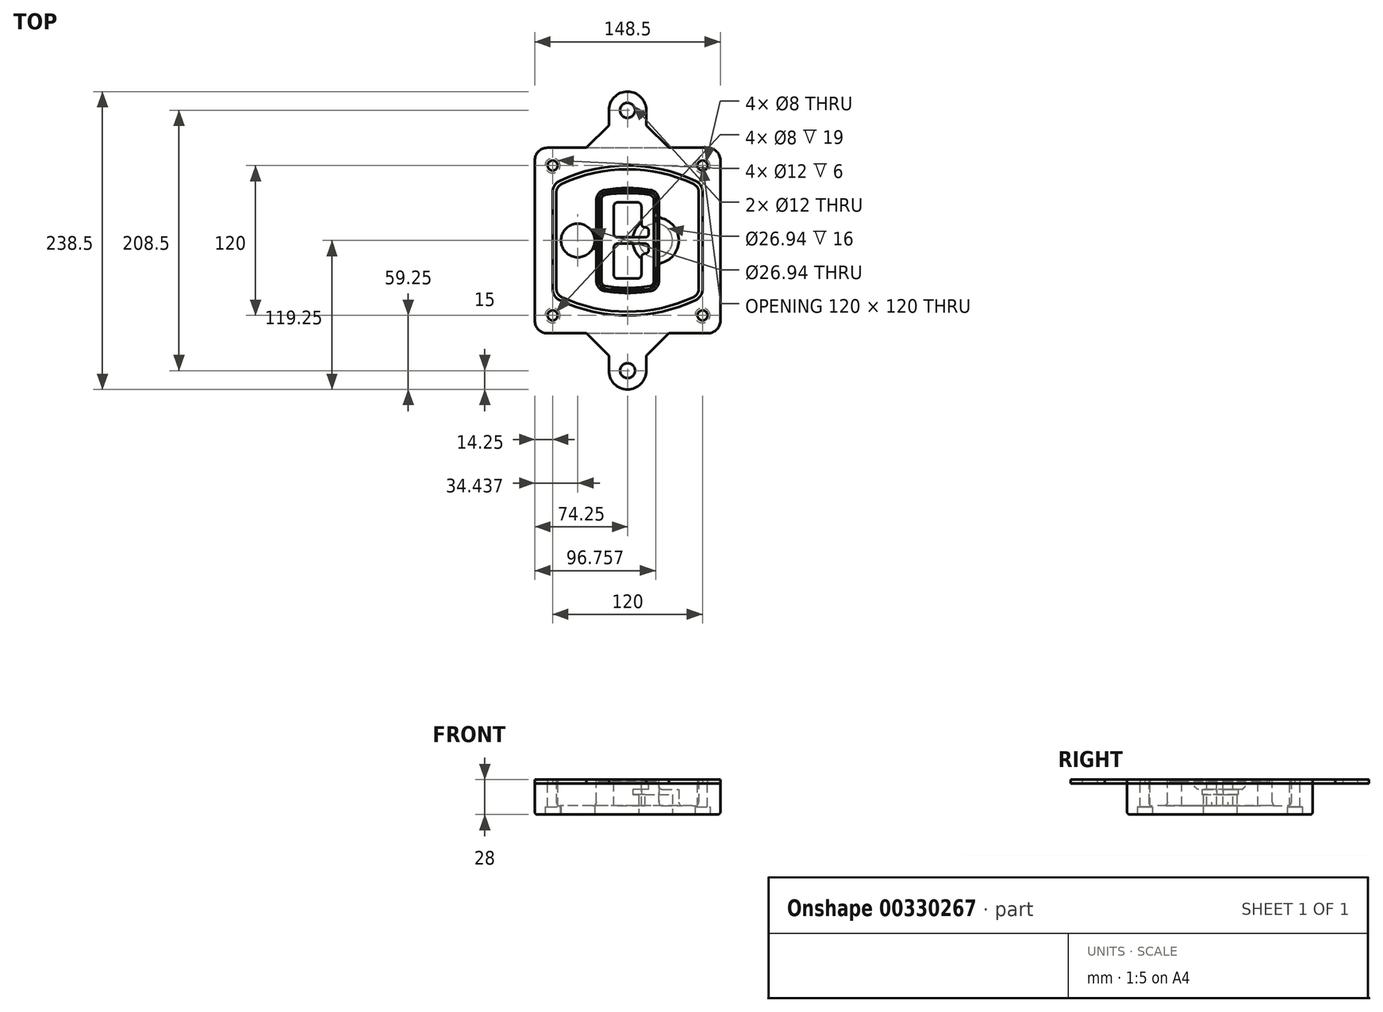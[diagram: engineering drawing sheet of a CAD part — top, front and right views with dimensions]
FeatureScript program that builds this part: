
annotation { "Feature Type Name" : "Feature", "Feature Type Description" : "" }
export const myFeature = defineFeature(function(context is Context, id is Id, definition is map)
    precondition{}
    {
        {
            var Q0;
            Q0=qCreatedBy(makeId("Top.planeOp"),FACE);
            var sketch = newSketch(context, id + "F0", { "sketchPlane" : qUnion([Q0])});
            skPoint(sketch, "E0.rect.middle", {"position": v(0, 0) * mm});
            skLineSegment(sketch, "E1.bottom", {"start": v(-64.25, -74.25) * mm, "end": v(64.25, -74.25) * mm});
            skLineSegment(sketch, "E1.top", {"start": v(-64.25, 74.25) * mm, "end": v(64.25, 74.25) * mm});
            skLineSegment(sketch, "E1.left", {"start": v(-74.25, -64.25) * mm, "end": v(-74.25, 64.25) * mm});
            skLineSegment(sketch, "E1.right", {"start": v(74.25, -64.25) * mm, "end": v(74.25, 64.25) * mm});
            skLineSegment(sketch, "E2", {"start": v(-74.25, 74.25) * mm, "end": v(74.25, -74.25) * mm, "construction": true});
            skLineSegment(sketch, "E3", {"start": v(74.25, 74.25) * mm, "end": v(-74.25, -74.25) * mm, "construction": true});
            skCircle(sketch, "E4", {"center": v(-60, 60) * mm, "radius": 4 * mm});
            skCircle(sketch, "E5", {"center": v(60, 60) * mm, "radius": 4 * mm});
            skCircle(sketch, "E6", {"center": v(60, -60) * mm, "radius": 4 * mm});
            skCircle(sketch, "E7", {"center": v(-60, -60) * mm, "radius": 4 * mm});
            skLineSegment(sketch, "E8", {"start": v(-60, 60) * mm, "end": v(60, 60) * mm, "construction": true});
            skLineSegment(sketch, "E9", {"start": v(60, 60) * mm, "end": v(60, -60) * mm, "construction": true});
            skLineSegment(sketch, "E10", {"start": v(60, -60) * mm, "end": v(-60, -60) * mm, "construction": true});
            skLineSegment(sketch, "E11", {"start": v(-60, -60) * mm, "end": v(-60, 60) * mm, "construction": true});
            skLineSegment(sketch, "E12", {"start": v(-60, 38.83) * mm, "end": v(-60, -38.83) * mm});
            skLineSegment(sketch, "E13", {"start": v(60, 38.83) * mm, "end": v(60, -38.83) * mm});
            skArc(sketch, "E14", {"start": v(54.26, 47.88) * mm, "mid": v(0, 60) * mm, "end": v(-54.26, 47.88) * mm});
            skArc(sketch, "E15", {"start": v(-54.26, -47.88) * mm, "mid": v(0, -60) * mm, "end": v(54.26, -47.88) * mm});
            skLineSegment(sketch, "E16", {"start": v(-60, 0) * mm, "end": v(60, 0) * mm, "construction": true});
            skPoint(sketch, "E17.visualSharp", {"position": v(-60, -45) * mm});
            skArc(sketch, "E17.filletArc", {"start": v(-60, -38.83) * mm, "mid": v(-58.44, -44.2) * mm, "end": v(-54.26, -47.88) * mm});
            skPoint(sketch, "E18.visualSharp", {"position": v(-60, 45) * mm});
            skArc(sketch, "E18.filletArc", {"start": v(-54.26, 47.88) * mm, "mid": v(-58.44, 44.2) * mm, "end": v(-60, 38.83) * mm});
            skPoint(sketch, "E19.visualSharp", {"position": v(60, 45) * mm});
            skArc(sketch, "E19.filletArc", {"start": v(60, 38.83) * mm, "mid": v(58.44, 44.2) * mm, "end": v(54.26, 47.88) * mm});
            skPoint(sketch, "E20.visualSharp", {"position": v(60, -45) * mm});
            skArc(sketch, "E20.filletArc", {"start": v(54.26, -47.88) * mm, "mid": v(58.44, -44.2) * mm, "end": v(60, -38.83) * mm});
            skPoint(sketch, "E21.visualSharp", {"position": v(-74.25, 74.25) * mm});
            skArc(sketch, "E21.filletArc", {"start": v(-64.25, 74.25) * mm, "mid": v(-71.32, 71.32) * mm, "end": v(-74.25, 64.25) * mm});
            skPoint(sketch, "E22.visualSharp", {"position": v(74.25, 74.25) * mm});
            skArc(sketch, "E22.filletArc", {"start": v(74.25, 64.25) * mm, "mid": v(71.32, 71.32) * mm, "end": v(64.25, 74.25) * mm});
            skPoint(sketch, "E23.visualSharp", {"position": v(74.25, -74.25) * mm});
            skArc(sketch, "E23.filletArc", {"start": v(64.25, -74.25) * mm, "mid": v(71.32, -71.32) * mm, "end": v(74.25, -64.25) * mm});
            skPoint(sketch, "E24.visualSharp", {"position": v(-74.25, -74.25) * mm});
            skArc(sketch, "E24.filletArc", {"start": v(-74.25, -64.25) * mm, "mid": v(-71.32, -71.32) * mm, "end": v(-64.25, -74.25) * mm});
            skArc(sketch, "E25.0", {"start": v(57, 38.83) * mm, "mid": v(55.9, 42.58) * mm, "end": v(52.98, 45.17) * mm});
            skLineSegment(sketch, "E25.1", {"start": v(57, 38.83) * mm, "end": v(57, -38.83) * mm});
            skArc(sketch, "E25.2", {"start": v(52.98, -45.17) * mm, "mid": v(55.9, -42.58) * mm, "end": v(57, -38.83) * mm});
            skArc(sketch, "E25.3", {"start": v(-52.98, -45.17) * mm, "mid": v(0, -57) * mm, "end": v(52.98, -45.17) * mm});
            skArc(sketch, "E25.4", {"start": v(-57, -38.83) * mm, "mid": v(-55.9, -42.58) * mm, "end": v(-52.98, -45.17) * mm});
            skArc(sketch, "E25.5", {"start": v(52.98, 45.17) * mm, "mid": v(0, 57) * mm, "end": v(-52.98, 45.17) * mm});
            skLineSegment(sketch, "E25.6", {"start": v(-57, 38.83) * mm, "end": v(-57, -38.83) * mm});
            skArc(sketch, "E25.7", {"start": v(-52.98, 45.17) * mm, "mid": v(-55.9, 42.58) * mm, "end": v(-57, 38.83) * mm});
            skArc(sketch, "E26.0", {"start": v(-55.96, 51.5) * mm, "mid": v(-61.82, 46.33) * mm, "end": v(-64, 38.83) * mm});
            skArc(sketch, "E26.1", {"start": v(55.96, 51.5) * mm, "mid": v(0, 64) * mm, "end": v(-55.96, 51.5) * mm});
            skArc(sketch, "E26.2", {"start": v(64, 38.83) * mm, "mid": v(61.82, 46.33) * mm, "end": v(55.96, 51.5) * mm});
            skLineSegment(sketch, "E26.3", {"start": v(64, 38.83) * mm, "end": v(64, -38.83) * mm});
            skArc(sketch, "E26.4", {"start": v(55.96, -51.5) * mm, "mid": v(61.82, -46.33) * mm, "end": v(64, -38.83) * mm});
            skLineSegment(sketch, "E26.5", {"start": v(-64, 38.83) * mm, "end": v(-64, -38.83) * mm});
            skArc(sketch, "E26.6", {"start": v(-55.96, -51.5) * mm, "mid": v(0, -64) * mm, "end": v(55.96, -51.5) * mm});
            skArc(sketch, "E26.7", {"start": v(-64, -38.83) * mm, "mid": v(-61.82, -46.33) * mm, "end": v(-55.96, -51.5) * mm});
            skSolve(sketch);
        }
        {
            var Q0;
            Q0=makeQuery(id+"F0.imprint","IMPRINT",FACE,{"disambiguationData":[TD([[makeQuery(id+"F0.imprint","IMPRINT",EDGE,{"derivedFrom":sQuery(id+"F0.wireOp",EDGE,"E1.bottom")}),1.0]])]});
            var Q1;
            Q1=makeQuery(id+"F0.imprint","IMPRINT",FACE,{"disambiguationData":[TD([[makeQuery(id+"F0.imprint","IMPRINT",EDGE,{"derivedFrom":sQuery(id+"F0.wireOp",EDGE,"E12")}),1.0]])]});
            var Q2;
            Q2=makeQuery(id+"F0.imprint","IMPRINT",FACE,{"disambiguationData":[TD([[makeQuery(id+"F0.imprint","IMPRINT",EDGE,{"derivedFrom":sQuery(id+"F0.wireOp",EDGE,"E25.0")}),1.0]])]});
            var Q3;
            Q3=makeQuery(id+"F0.imprint","IMPRINT",FACE,{"disambiguationData":[TD([[makeQuery(id+"F0.imprint","IMPRINT",EDGE,{"derivedFrom":sQuery(id+"F0.wireOp",EDGE,"E12")}),-1.0]])]});
            extrude(context, id + "F1", {"entities" : qUnion([Q0, Q1, Q2, Q3]), "oppositeDirection" : true, "depth" : 25 * mm});
        }
        {
            var Q0;
            Q0=makeQuery(id+"F0.imprint","IMPRINT",FACE,{"disambiguationData":[TD([[makeQuery(id+"F0.imprint","IMPRINT",EDGE,{"derivedFrom":sQuery(id+"F0.wireOp",EDGE,"E12")}),1.0]])]});
            extrude(context, id + "F2", {"entities" : qUnion([Q0]), "operationType" : NewBodyOperationType.ADD, "depth" : 3 * mm});
        }
        {
            var Q0;
            Q0=makeQuery(id+"F0.imprint","IMPRINT",FACE,{"disambiguationData":[TD([[makeQuery(id+"F0.imprint","IMPRINT",EDGE,{"derivedFrom":sQuery(id+"F0.wireOp",EDGE,"E25.0")}),1.0]])]});
            extrude(context, id + "F3", {"entities" : qUnion([Q0]), "operationType" : NewBodyOperationType.REMOVE, "oppositeDirection" : true, "depth" : 18 * mm});
        }
        {
            var Q0;
            Q0=makeQuery(id+"F2.opExtrude","CAP_FACE",FACE,{"disambiguationData":[OSD([sQuery(id+"F0.wireOp",EDGE,"E12"),sQuery(id+"F0.wireOp",EDGE,"E13"),sQuery(id+"F0.wireOp",EDGE,"E14"),sQuery(id+"F0.wireOp",EDGE,"E15"),sQuery(id+"F0.wireOp",EDGE,"E17.filletArc"),sQuery(id+"F0.wireOp",EDGE,"E18.filletArc"),sQuery(id+"F0.wireOp",EDGE,"E19.filletArc"),sQuery(id+"F0.wireOp",EDGE,"E20.filletArc"),sQuery(id+"F0.wireOp",EDGE,"E25.0"),sQuery(id+"F0.wireOp",EDGE,"E25.1"),sQuery(id+"F0.wireOp",EDGE,"E25.2"),sQuery(id+"F0.wireOp",EDGE,"E25.3"),sQuery(id+"F0.wireOp",EDGE,"E25.4"),sQuery(id+"F0.wireOp",EDGE,"E25.5"),sQuery(id+"F0.wireOp",EDGE,"E25.6"),sQuery(id+"F0.wireOp",EDGE,"E25.7")])],"isStart":false});
            var sketch = newSketch(context, id + "F4", { "sketchPlane" : qUnion([Q0])});
            skArc(sketch, "E27.0", {"start": v(-18.34, -40.45) * mm, "mid": v(0, -42) * mm, "end": v(18.34, -40.45) * mm});
            skArc(sketch, "E28.0", {"start": v(18.34, 40.45) * mm, "mid": v(0, 42) * mm, "end": v(-18.34, 40.45) * mm});
            skLineSegment(sketch, "E29", {"start": v(-25, 32.57) * mm, "end": v(-25, -32.57) * mm});
            skLineSegment(sketch, "E30", {"start": v(25, 32.57) * mm, "end": v(25, -32.57) * mm});
            skLineSegment(sketch, "E31", {"start": v(-25, 39.1) * mm, "end": v(25, 39.1) * mm, "construction": true});
            skLineSegment(sketch, "E32", {"start": v(-25, -39.1) * mm, "end": v(25, -39.1) * mm, "construction": true});
            skPoint(sketch, "E33.visualSharp", {"position": v(-25, 39.1) * mm});
            skArc(sketch, "E33.filletArc", {"start": v(-18.34, 40.45) * mm, "mid": v(-23.11, 37.73) * mm, "end": v(-25, 32.57) * mm});
            skPoint(sketch, "E34.visualSharp", {"position": v(25, 39.1) * mm});
            skArc(sketch, "E34.filletArc", {"start": v(25, 32.57) * mm, "mid": v(23.11, 37.73) * mm, "end": v(18.34, 40.45) * mm});
            skPoint(sketch, "E35.visualSharp", {"position": v(25, -39.1) * mm});
            skArc(sketch, "E35.filletArc", {"start": v(18.34, -40.45) * mm, "mid": v(23.11, -37.73) * mm, "end": v(25, -32.57) * mm});
            skPoint(sketch, "E36.visualSharp", {"position": v(-25, -39.1) * mm});
            skArc(sketch, "E36.filletArc", {"start": v(-25, -32.57) * mm, "mid": v(-23.11, -37.73) * mm, "end": v(-18.34, -40.45) * mm});
            skArc(sketch, "E37.0", {"start": v(52.98, 45.17) * mm, "mid": v(0, 57) * mm, "end": v(-52.98, 45.17) * mm});
            skArc(sketch, "E37.1", {"start": v(-52.98, 45.17) * mm, "mid": v(-55.9, 42.58) * mm, "end": v(-57, 38.83) * mm});
            skLineSegment(sketch, "E37.2", {"start": v(-57, 38.83) * mm, "end": v(-57, -38.83) * mm});
            skArc(sketch, "E37.3", {"start": v(-57, -38.83) * mm, "mid": v(-55.9, -42.58) * mm, "end": v(-52.98, -45.17) * mm});
            skArc(sketch, "E37.4", {"start": v(-52.98, -45.17) * mm, "mid": v(0, -57) * mm, "end": v(52.98, -45.17) * mm});
            skArc(sketch, "E37.5", {"start": v(52.98, -45.17) * mm, "mid": v(55.9, -42.58) * mm, "end": v(57, -38.83) * mm});
            skLineSegment(sketch, "E37.6", {"start": v(57, 38.83) * mm, "end": v(57, -38.83) * mm});
            skArc(sketch, "E37.7", {"start": v(57, 38.83) * mm, "mid": v(55.9, 42.58) * mm, "end": v(52.98, 45.17) * mm});
            skLineSegment(sketch, "E38.0", {"start": v(23, 32.57) * mm, "end": v(23, -32.57) * mm});
            skArc(sketch, "E38.1", {"start": v(18, -38.48) * mm, "mid": v(21.58, -36.44) * mm, "end": v(23, -32.57) * mm});
            skArc(sketch, "E38.2", {"start": v(-18, -38.48) * mm, "mid": v(0, -40) * mm, "end": v(18, -38.48) * mm});
            skArc(sketch, "E38.3", {"start": v(-23, -32.57) * mm, "mid": v(-21.58, -36.44) * mm, "end": v(-18, -38.48) * mm});
            skLineSegment(sketch, "E38.4", {"start": v(-23, 32.57) * mm, "end": v(-23, -32.57) * mm});
            skArc(sketch, "E38.5", {"start": v(23, 32.57) * mm, "mid": v(21.58, 36.44) * mm, "end": v(18, 38.48) * mm});
            skArc(sketch, "E38.6", {"start": v(-18, 38.48) * mm, "mid": v(-21.58, 36.44) * mm, "end": v(-23, 32.57) * mm});
            skArc(sketch, "E38.7", {"start": v(18, 38.48) * mm, "mid": v(0, 40) * mm, "end": v(-18, 38.48) * mm});
            skArc(sketch, "E39.0", {"start": v(21, 32.57) * mm, "mid": v(20.06, 35.15) * mm, "end": v(17.67, 36.5) * mm});
            skLineSegment(sketch, "E39.1", {"start": v(21, 32.57) * mm, "end": v(21, -32.57) * mm});
            skArc(sketch, "E39.2", {"start": v(17.67, -36.5) * mm, "mid": v(20.06, -35.15) * mm, "end": v(21, -32.57) * mm});
            skArc(sketch, "E39.3", {"start": v(-17.67, -36.5) * mm, "mid": v(0, -38) * mm, "end": v(17.67, -36.5) * mm});
            skArc(sketch, "E39.4", {"start": v(-21, -32.57) * mm, "mid": v(-20.06, -35.15) * mm, "end": v(-17.67, -36.5) * mm});
            skArc(sketch, "E39.5", {"start": v(17.67, 36.5) * mm, "mid": v(0, 38) * mm, "end": v(-17.67, 36.5) * mm});
            skLineSegment(sketch, "E39.6", {"start": v(-21, 32.57) * mm, "end": v(-21, -32.57) * mm});
            skArc(sketch, "E39.7", {"start": v(-17.67, 36.5) * mm, "mid": v(-20.06, 35.15) * mm, "end": v(-21, 32.57) * mm});
            skLineSegment(sketch, "E40", {"start": v(-25, 0) * mm, "end": v(25, 0) * mm, "construction": true});
            skLineSegment(sketch, "E41", {"start": v(-11, 5.5) * mm, "end": v(-11, 27.5) * mm});
            skLineSegment(sketch, "E42", {"start": v(-8, 30.5) * mm, "end": v(8, 30.5) * mm});
            skLineSegment(sketch, "E43", {"start": v(11, 27.5) * mm, "end": v(11, 13.5) * mm});
            skLineSegment(sketch, "E44", {"start": v(14, 10.5) * mm, "end": v(14, 10.5) * mm});
            skLineSegment(sketch, "E45", {"start": v(17, 7.5) * mm, "end": v(17, 5.5) * mm});
            skLineSegment(sketch, "E46", {"start": v(14, 2.5) * mm, "end": v(-8, 2.5) * mm});
            skPoint(sketch, "E47.visualSharp", {"position": v(-11, 30.5) * mm});
            skArc(sketch, "E47.filletArc", {"start": v(-8, 30.5) * mm, "mid": v(-10.12, 29.62) * mm, "end": v(-11, 27.5) * mm});
            skPoint(sketch, "E48.visualSharp", {"position": v(11, 30.5) * mm});
            skArc(sketch, "E48.filletArc", {"start": v(11, 27.5) * mm, "mid": v(10.12, 29.62) * mm, "end": v(8, 30.5) * mm});
            skPoint(sketch, "E49.visualSharp", {"position": v(11, 10.5) * mm});
            skArc(sketch, "E49.filletArc", {"start": v(11, 13.5) * mm, "mid": v(11.88, 11.38) * mm, "end": v(14, 10.5) * mm});
            skPoint(sketch, "E50.visualSharp", {"position": v(17, 10.5) * mm});
            skArc(sketch, "E50.filletArc", {"start": v(17, 7.5) * mm, "mid": v(16.12, 9.62) * mm, "end": v(14, 10.5) * mm});
            skPoint(sketch, "E51.visualSharp", {"position": v(17, 2.5) * mm});
            skArc(sketch, "E51.filletArc", {"start": v(14, 2.5) * mm, "mid": v(16.12, 3.38) * mm, "end": v(17, 5.5) * mm});
            skPoint(sketch, "E52.visualSharp", {"position": v(-11, 2.5) * mm});
            skArc(sketch, "E52.filletArc", {"start": v(-11, 5.5) * mm, "mid": v(-10.12, 3.38) * mm, "end": v(-8, 2.5) * mm});
            skLineSegment(sketch, "E53.0.MirrorCS", {"start": v(14, -2.5) * mm, "end": v(-8, -2.5) * mm});
            skArc(sketch, "E54.0.MirrorCS", {"start": v(-11, -5.5) * mm, "mid": v(-10.12, -3.38) * mm, "end": v(-8, -2.5) * mm});
            skLineSegment(sketch, "E55.0.MirrorCS", {"start": v(-11, -5.5) * mm, "end": v(-11, -27.5) * mm});
            skArc(sketch, "E56.0.MirrorCS", {"start": v(-8, -30.5) * mm, "mid": v(-10.12, -29.62) * mm, "end": v(-11, -27.5) * mm});
            skLineSegment(sketch, "E57.0.MirrorCS", {"start": v(-8, -30.5) * mm, "end": v(8, -30.5) * mm});
            skArc(sketch, "E58.0.MirrorCS", {"start": v(11, -27.5) * mm, "mid": v(10.12, -29.62) * mm, "end": v(8, -30.5) * mm});
            skLineSegment(sketch, "E59.0.MirrorCS", {"start": v(11, -27.5) * mm, "end": v(11, -13.5) * mm});
            skArc(sketch, "E60.0.MirrorCS", {"start": v(11, -13.5) * mm, "mid": v(11.88, -11.38) * mm, "end": v(14, -10.5) * mm});
            skArc(sketch, "E61.0.MirrorCS", {"start": v(17, -7.5) * mm, "mid": v(16.12, -9.62) * mm, "end": v(14, -10.5) * mm});
            skLineSegment(sketch, "E62.0.MirrorCS", {"start": v(17, -7.5) * mm, "end": v(17, -5.5) * mm});
            skArc(sketch, "E63.0.MirrorCS", {"start": v(14, -2.5) * mm, "mid": v(16.12, -3.38) * mm, "end": v(17, -5.5) * mm});
            skSolve(sketch);
        }
        {
            var Q0;
            Q0=makeQuery(id+"F4.imprint","IMPRINT",FACE,{"disambiguationData":[TD([[makeQuery(id+"F4.imprint","IMPRINT",EDGE,{"derivedFrom":sQuery(id+"F4.wireOp",EDGE,"E27.0")}),1.0]])]});
            var Q1;
            Q1=makeQuery(id+"F4.imprint","IMPRINT",FACE,{"disambiguationData":[TD([[makeQuery(id+"F4.imprint","IMPRINT",EDGE,{"derivedFrom":sQuery(id+"F4.wireOp",EDGE,"E38.0")}),-1.0]])]});
            var Q2;
            Q2=makeQuery(id+"F4.imprint","IMPRINT",FACE,{"disambiguationData":[TD([[makeQuery(id+"F4.imprint","IMPRINT",EDGE,{"derivedFrom":sQuery(id+"F4.wireOp",EDGE,"E39.0")}),1.0]])]});
            extrude(context, id + "F5", {"entities" : qUnion([Q0, Q1, Q2]), "operationType" : NewBodyOperationType.ADD, "endBound" : BoundingType.UP_TO_NEXT, "oppositeDirection" : true, "depth" : 25 * mm});
        }
        {
            var Q0;
            Q0=makeQuery(id+"F4.imprint","IMPRINT",FACE,{"disambiguationData":[TD([[makeQuery(id+"F4.imprint","IMPRINT",EDGE,{"derivedFrom":sQuery(id+"F4.wireOp",EDGE,"E38.0")}),-1.0]])]});
            extrude(context, id + "F6", {"entities" : qUnion([Q0]), "operationType" : NewBodyOperationType.REMOVE, "oppositeDirection" : true, "depth" : 2 * mm});
        }
        {
            var Q0;
            Q0=makeQuery(id+"F1.opExtrude","CAP_FACE",FACE,{"disambiguationData":[OSD([sQuery(id+"F0.wireOp",EDGE,"E1.bottom"),sQuery(id+"F0.wireOp",EDGE,"E1.top"),sQuery(id+"F0.wireOp",EDGE,"E1.left"),sQuery(id+"F0.wireOp",EDGE,"E1.right"),sQuery(id+"F0.wireOp",EDGE,"E4"),sQuery(id+"F0.wireOp",EDGE,"E5"),sQuery(id+"F0.wireOp",EDGE,"E6"),sQuery(id+"F0.wireOp",EDGE,"E7"),sQuery(id+"F0.wireOp",EDGE,"E21.filletArc"),sQuery(id+"F0.wireOp",EDGE,"E22.filletArc"),sQuery(id+"F0.wireOp",EDGE,"E23.filletArc"),sQuery(id+"F0.wireOp",EDGE,"E24.filletArc")])],"isStart":false});
            var sketch = newSketch(context, id + "F7", { "sketchPlane" : qUnion([Q0])});
            skCircle(sketch, "E64", {"center": v(22.5, 0) * mm, "radius": 13.47 * mm});
            skCircle(sketch, "E65", {"center": v(-39.81, 0) * mm, "radius": 13.47 * mm});
            skLineSegment(sketch, "E66", {"start": v(74.25, 0) * mm, "end": v(-74.25, 0) * mm});
            skCircle(sketch, "E67", {"center": v(22.5, 0) * mm, "radius": 18.47 * mm});
            skCircle(sketch, "E68", {"center": v(60, -60) * mm, "radius": 6 * mm});
            skCircle(sketch, "E69", {"center": v(-60, -60) * mm, "radius": 6 * mm});
            skCircle(sketch, "E70", {"center": v(-60, 60) * mm, "radius": 6 * mm});
            skCircle(sketch, "E71", {"center": v(60, 60) * mm, "radius": 6 * mm});
            skSolve(sketch);
        }
        {
            var Q0;
            {var subQ1=sQuery(id+"F7.wireOp",EDGE,"E66");var subQ4=sQuery(id+"F7.wireOp",EDGE,"E64");var subQ6=makeQuery(id+"F7.imprint","INTERSECT",VERTEX,{"disambiguationData":[OD(0.0)],"derivedFrom":[subQ4,subQ1]});Q0=makeQuery(id+"F7.imprint","IMPRINT",FACE,{"disambiguationData":[TD([[makeQuery(id+"F7.imprint","IMPRINT",EDGE,{"disambiguationData":[TD([[subQ6,-1.0]])],"derivedFrom":subQ4}),-1.0]])]});}
            var Q1;
            {var subQ0=sQuery(id+"F7.wireOp",EDGE,"E66");var subQ1=sQuery(id+"F7.wireOp",EDGE,"E64");var subQ3=makeQuery(id+"F7.imprint","INTERSECT",VERTEX,{"disambiguationData":[OD(0.0)],"derivedFrom":[subQ1,subQ0]});Q1=makeQuery(id+"F7.imprint","IMPRINT",FACE,{"disambiguationData":[TD([[makeQuery(id+"F7.imprint","IMPRINT",EDGE,{"disambiguationData":[TD([[subQ3,-1.0]])],"derivedFrom":subQ1}),1.0]])]});}
            var Q2;
            {var subQ0=sQuery(id+"F7.wireOp",EDGE,"E66");var subQ1=sQuery(id+"F7.wireOp",EDGE,"E64");var subQ3=makeQuery(id+"F7.imprint","INTERSECT",VERTEX,{"disambiguationData":[OD(0.0)],"derivedFrom":[subQ1,subQ0]});Q2=makeQuery(id+"F7.imprint","IMPRINT",FACE,{"disambiguationData":[TD([[makeQuery(id+"F7.imprint","IMPRINT",EDGE,{"disambiguationData":[TD([[subQ3,1.0]])],"derivedFrom":subQ1}),1.0]])]});}
            var Q3;
            {var subQ1=sQuery(id+"F7.wireOp",EDGE,"E66");var subQ4=sQuery(id+"F7.wireOp",EDGE,"E64");var subQ6=makeQuery(id+"F7.imprint","INTERSECT",VERTEX,{"disambiguationData":[OD(0.0)],"derivedFrom":[subQ4,subQ1]});Q3=makeQuery(id+"F7.imprint","IMPRINT",FACE,{"disambiguationData":[TD([[makeQuery(id+"F7.imprint","IMPRINT",EDGE,{"disambiguationData":[TD([[subQ6,1.0]])],"derivedFrom":subQ4}),-1.0]])]});}
            extrude(context, id + "F8", {"entities" : qUnion([Q0, Q1, Q2, Q3]), "operationType" : NewBodyOperationType.ADD, "oppositeDirection" : true, "depth" : 20 * mm});
        }
        {
            var Q0;
            {var subQ0=sQuery(id+"F7.wireOp",EDGE,"E66");var subQ1=sQuery(id+"F7.wireOp",EDGE,"E64");var subQ3=makeQuery(id+"F7.imprint","INTERSECT",VERTEX,{"disambiguationData":[OD(0.0)],"derivedFrom":[subQ1,subQ0]});Q0=makeQuery(id+"F7.imprint","IMPRINT",FACE,{"disambiguationData":[TD([[makeQuery(id+"F7.imprint","IMPRINT",EDGE,{"disambiguationData":[TD([[subQ3,-1.0]])],"derivedFrom":subQ1}),1.0]])]});}
            var Q1;
            {var subQ0=sQuery(id+"F7.wireOp",EDGE,"E66");var subQ1=sQuery(id+"F7.wireOp",EDGE,"E64");var subQ3=makeQuery(id+"F7.imprint","INTERSECT",VERTEX,{"disambiguationData":[OD(0.0)],"derivedFrom":[subQ1,subQ0]});Q1=makeQuery(id+"F7.imprint","IMPRINT",FACE,{"disambiguationData":[TD([[makeQuery(id+"F7.imprint","IMPRINT",EDGE,{"disambiguationData":[TD([[subQ3,1.0]])],"derivedFrom":subQ1}),1.0]])]});}
            extrude(context, id + "F9", {"entities" : qUnion([Q0, Q1]), "operationType" : NewBodyOperationType.REMOVE, "oppositeDirection" : true, "depth" : 16 * mm});
        }
        {
            var Q0;
            {var subQ0=sQuery(id+"F7.wireOp",EDGE,"E66");var subQ1=sQuery(id+"F7.wireOp",EDGE,"E65");var subQ3=makeQuery(id+"F7.imprint","INTERSECT",VERTEX,{"disambiguationData":[OD(0.0)],"derivedFrom":[subQ1,subQ0]});Q0=makeQuery(id+"F7.imprint","IMPRINT",FACE,{"disambiguationData":[TD([[makeQuery(id+"F7.imprint","IMPRINT",EDGE,{"disambiguationData":[TD([[subQ3,-1.0]])],"derivedFrom":subQ1}),1.0]])]});}
            var Q1;
            {var subQ0=sQuery(id+"F7.wireOp",EDGE,"E66");var subQ1=sQuery(id+"F7.wireOp",EDGE,"E65");var subQ3=makeQuery(id+"F7.imprint","INTERSECT",VERTEX,{"disambiguationData":[OD(0.0)],"derivedFrom":[subQ1,subQ0]});Q1=makeQuery(id+"F7.imprint","IMPRINT",FACE,{"disambiguationData":[TD([[makeQuery(id+"F7.imprint","IMPRINT",EDGE,{"disambiguationData":[TD([[subQ3,1.0]])],"derivedFrom":subQ1}),1.0]])]});}
            extrude(context, id + "F10", {"entities" : qUnion([Q0, Q1]), "operationType" : NewBodyOperationType.REMOVE, "oppositeDirection" : true, "depth" : 25 * mm});
        }
        {
            var Q0;
            Q0=makeQuery(id+"F7.imprint","IMPRINT",FACE,{"disambiguationData":[TD([[makeQuery(id+"F7.imprint","IMPRINT",EDGE,{"derivedFrom":sQuery(id+"F7.wireOp",EDGE,"E68")}),1.0]])]});
            var Q1;
            Q1=makeQuery(id+"F7.imprint","IMPRINT",FACE,{"disambiguationData":[TD([[makeQuery(id+"F7.imprint","IMPRINT",EDGE,{"derivedFrom":makeQuery(id+"F1.opExtrude","CAP_EDGE",EDGE,{"disambiguationData":[OSD([sQuery(id+"F0.wireOp",EDGE,"E5")])],"isStart":false})}),-1.0]])]});
            var Q2;
            Q2=makeQuery(id+"F7.imprint","IMPRINT",FACE,{"disambiguationData":[TD([[makeQuery(id+"F7.imprint","IMPRINT",EDGE,{"derivedFrom":sQuery(id+"F7.wireOp",EDGE,"E69")}),1.0]])]});
            var Q3;
            Q3=makeQuery(id+"F7.imprint","IMPRINT",FACE,{"disambiguationData":[TD([[makeQuery(id+"F7.imprint","IMPRINT",EDGE,{"derivedFrom":makeQuery(id+"F1.opExtrude","CAP_EDGE",EDGE,{"disambiguationData":[OSD([sQuery(id+"F0.wireOp",EDGE,"E4")])],"isStart":false})}),-1.0]])]});
            var Q4;
            Q4=makeQuery(id+"F7.imprint","IMPRINT",FACE,{"disambiguationData":[TD([[makeQuery(id+"F7.imprint","IMPRINT",EDGE,{"derivedFrom":sQuery(id+"F7.wireOp",EDGE,"E70")}),1.0]])]});
            var Q5;
            Q5=makeQuery(id+"F7.imprint","IMPRINT",FACE,{"disambiguationData":[TD([[makeQuery(id+"F7.imprint","IMPRINT",EDGE,{"derivedFrom":makeQuery(id+"F1.opExtrude","CAP_EDGE",EDGE,{"disambiguationData":[OSD([sQuery(id+"F0.wireOp",EDGE,"E7")])],"isStart":false})}),-1.0]])]});
            var Q6;
            Q6=makeQuery(id+"F7.imprint","IMPRINT",FACE,{"disambiguationData":[TD([[makeQuery(id+"F7.imprint","IMPRINT",EDGE,{"derivedFrom":sQuery(id+"F7.wireOp",EDGE,"E71")}),1.0]])]});
            var Q7;
            Q7=makeQuery(id+"F7.imprint","IMPRINT",FACE,{"disambiguationData":[TD([[makeQuery(id+"F7.imprint","IMPRINT",EDGE,{"derivedFrom":makeQuery(id+"F1.opExtrude","CAP_EDGE",EDGE,{"disambiguationData":[OSD([sQuery(id+"F0.wireOp",EDGE,"E6")])],"isStart":false})}),-1.0]])]});
            extrude(context, id + "F11", {"entities" : qUnion([Q0, Q1, Q2, Q3, Q4, Q5, Q6, Q7]), "operationType" : NewBodyOperationType.REMOVE, "oppositeDirection" : true, "depth" : 6 * mm});
        }
        {
            var Q0;
            Q0=makeQuery(id+"F9.boolean.opBoolean","COPY",FACE,{"derivedFrom":makeQuery(id+"F9.opExtrude","CAP_FACE",FACE,{"disambiguationData":[OSD([sQuery(id+"F7.wireOp",EDGE,"E64")])],"isStart":false})});
            var sketch = newSketch(context, id + "F12", { "sketchPlane" : qUnion([Q0])});
            skArc(sketch, "E72.0", {"start": v(11, 14.45) * mm, "mid": v(6.45, 9.13) * mm, "end": v(4.2, 2.5) * mm});
            skArc(sketch, "E72.1", {"start": v(4.2, -2.5) * mm, "mid": v(6.45, -9.13) * mm, "end": v(11, -14.45) * mm});
            skLineSegment(sketch, "E73", {"start": v(4.2, -2.5) * mm, "end": v(14, -2.5) * mm});
            skLineSegment(sketch, "E74.0", {"start": v(14, 2.5) * mm, "end": v(4.2, 2.5) * mm});
            skArc(sketch, "E74.1", {"start": v(14, 2.5) * mm, "mid": v(16.12, 3.38) * mm, "end": v(17, 5.5) * mm});
            skLineSegment(sketch, "E74.2", {"start": v(17, 7.5) * mm, "end": v(17, 5.5) * mm});
            skArc(sketch, "E74.3", {"start": v(17, 7.5) * mm, "mid": v(16.12, 9.62) * mm, "end": v(14, 10.5) * mm});
            skArc(sketch, "E74.4", {"start": v(11, 13.5) * mm, "mid": v(11.88, 11.38) * mm, "end": v(14, 10.5) * mm});
            skLineSegment(sketch, "E74.5", {"start": v(11, 14.45) * mm, "end": v(11, 13.5) * mm});
            skLineSegment(sketch, "E74.7", {"start": v(14, -2.5) * mm, "end": v(4.2, -2.5) * mm});
            skArc(sketch, "E74.8", {"start": v(14, -2.5) * mm, "mid": v(16.12, -3.38) * mm, "end": v(17, -5.5) * mm});
            skLineSegment(sketch, "E74.9", {"start": v(17, -7.5) * mm, "end": v(17, -5.5) * mm});
            skArc(sketch, "E74.10", {"start": v(17, -7.5) * mm, "mid": v(16.12, -9.62) * mm, "end": v(14, -10.5) * mm});
            skArc(sketch, "E74.11", {"start": v(11, -13.5) * mm, "mid": v(11.88, -11.38) * mm, "end": v(14, -10.5) * mm});
            skLineSegment(sketch, "E74.12", {"start": v(11, -14.45) * mm, "end": v(11, -13.5) * mm});
            skPoint(sketch, "E75.orphan", {"position": v(11, -27.5) * mm});
            skPoint(sketch, "E76.orphan", {"position": v(-8, -2.5) * mm});
            skPoint(sketch, "E77.orphan", {"position": v(-8, 2.5) * mm});
            skPoint(sketch, "E78.orphan", {"position": v(11, 27.5) * mm});
            skSolve(sketch);
        }
        {
            var Q0;
            {var subQ7=sQuery(id+"F12.wireOp",EDGE,"E72.0");var subQ14=sQuery(id+"F12.wireOp",EDGE,"E72.1");var subQ16=sQuery(id+"F12.wireOp",EDGE,"E74.1");var subQ18=sQuery(id+"F12.wireOp",EDGE,"E74.8");Q0=qUnion([makeQuery(id+"F12.imprint","IMPRINT",FACE,{"disambiguationData":[TD([[makeQuery(id+"F12.imprint","IMPRINT",EDGE,{"derivedFrom":subQ7}),1.0]])]}),makeQuery(id+"F12.imprint","IMPRINT",FACE,{"disambiguationData":[TD([[makeQuery(id+"F12.imprint","IMPRINT",EDGE,{"derivedFrom":subQ14}),1.0]])]}),makeQuery(id+"F12.imprint","IMPRINT",FACE,{"disambiguationData":[TD([[makeQuery(id+"F12.imprint","IMPRINT",EDGE,{"derivedFrom":subQ16}),1.0]])]}),makeQuery(id+"F12.imprint","IMPRINT",FACE,{"disambiguationData":[TD([[makeQuery(id+"F12.imprint","IMPRINT",EDGE,{"derivedFrom":subQ18}),-1.0]])]})]);}
            var Q1;
            Q1=makeQuery(id+"F5.boolean.opBoolean","SPLIT",FACE,{"disambiguationData":[TD([makeQuery(id+"F5.opExtrude","SWEPT_FACE",FACE,{"disambiguationData":[OSD([sQuery(id+"F4.wireOp",EDGE,"E41")])]})])],"derivedFrom":makeQuery(id+"F3.boolean.opBoolean","COPY",FACE,{"derivedFrom":makeQuery(id+"F3.opExtrude","CAP_FACE",FACE,{"disambiguationData":[OSD([sQuery(id+"F0.wireOp",EDGE,"E25.0"),sQuery(id+"F0.wireOp",EDGE,"E25.1"),sQuery(id+"F0.wireOp",EDGE,"E25.2"),sQuery(id+"F0.wireOp",EDGE,"E25.3"),sQuery(id+"F0.wireOp",EDGE,"E25.4"),sQuery(id+"F0.wireOp",EDGE,"E25.5"),sQuery(id+"F0.wireOp",EDGE,"E25.6"),sQuery(id+"F0.wireOp",EDGE,"E25.7")])],"isStart":false})})});
            extrude(context, id + "F13", {"entities" : qUnion([Q0]), "operationType" : NewBodyOperationType.REMOVE, "endBound" : BoundingType.UP_TO_SURFACE, "endBoundEntityFace" : qUnion([Q1]), "depth" : 25 * mm});
        }
        {
            var Q0;
            Q0=makeQuery(id+"F3.boolean.opBoolean","COPY",EDGE,{"derivedFrom":makeQuery(id+"F3.opExtrude","CAP_EDGE",EDGE,{"disambiguationData":[OSD([sQuery(id+"F0.wireOp",EDGE,"E25.6")])],"isStart":false})});
            var Q1;
            Q1=makeQuery(id+"F8.boolean.opBoolean","INTERSECT",EDGE,{"derivedFrom":[makeQuery(id+"F5.opExtrude","SWEPT_FACE",FACE,{"disambiguationData":[OSD([sQuery(id+"F4.wireOp",EDGE,"E30")])]}),makeQuery(id+"F8.opExtrude","CAP_FACE",FACE,{"disambiguationData":[OSD([sQuery(id+"F7.wireOp",EDGE,"E67")])],"isStart":false})]});
            var Q2;
            Q2=makeQuery(id+"F8.boolean.opBoolean","INTERSECT",EDGE,{"disambiguationData":[OD(1.0)],"derivedFrom":[makeQuery(id+"F5.opExtrude","SWEPT_FACE",FACE,{"disambiguationData":[OSD([sQuery(id+"F4.wireOp",EDGE,"E30")])]}),makeQuery(id+"F8.opExtrude","SWEPT_FACE",FACE,{"disambiguationData":[OSD([sQuery(id+"F7.wireOp",EDGE,"E67")])]})]});
            var Q3;
            {var subQ0=sQuery(id+"F4.wireOp",EDGE,"E30");Q3=makeQuery(id+"F8.boolean.opBoolean","SPLIT",EDGE,{"disambiguationData":[TD([makeQuery(id+"F5.opExtrude","SWEPT_FACE",FACE,{"disambiguationData":[OSD([sQuery(id+"F4.wireOp",EDGE,"E35.filletArc")])]})])],"derivedFrom":makeQuery(id+"F5.opExtrude","CAP_EDGE",EDGE,{"disambiguationData":[OSD([subQ0])],"isStart":false})});}
            var Q4;
            {var subQ0=sQuery(id+"F0.wireOp",EDGE,"E25.7");var subQ1=sQuery(id+"F0.wireOp",EDGE,"E25.1");var subQ2=sQuery(id+"F0.wireOp",EDGE,"E25.6");var subQ3=sQuery(id+"F0.wireOp",EDGE,"E25.5");var subQ4=sQuery(id+"F0.wireOp",EDGE,"E25.4");var subQ5=sQuery(id+"F0.wireOp",EDGE,"E25.0");var subQ6=sQuery(id+"F0.wireOp",EDGE,"E25.2");var subQ7=sQuery(id+"F0.wireOp",EDGE,"E25.3");Q4=makeQuery(id+"F8.boolean.opBoolean","INTERSECT",EDGE,{"derivedFrom":[makeQuery(id+"F5.boolean.opBoolean","SPLIT",FACE,{"disambiguationData":[TD([makeQuery(id+"F2.opExtrude","SWEPT_FACE",FACE,{"disambiguationData":[OSD([subQ5])]})])],"derivedFrom":makeQuery(id+"F3.boolean.opBoolean","COPY",FACE,{"derivedFrom":makeQuery(id+"F3.opExtrude","CAP_FACE",FACE,{"disambiguationData":[OSD([subQ5,subQ1,subQ6,subQ7,subQ4,subQ3,subQ2,subQ0])],"isStart":false})})}),makeQuery(id+"F8.opExtrude","SWEPT_FACE",FACE,{"disambiguationData":[OSD([sQuery(id+"F7.wireOp",EDGE,"E67")])]})]});}
            var Q5;
            Q5=makeQuery(id+"F8.boolean.opBoolean","INTERSECT",EDGE,{"disambiguationData":[OD(0.0)],"derivedFrom":[makeQuery(id+"F5.opExtrude","SWEPT_FACE",FACE,{"disambiguationData":[OSD([sQuery(id+"F4.wireOp",EDGE,"E30")])]}),makeQuery(id+"F8.opExtrude","SWEPT_FACE",FACE,{"disambiguationData":[OSD([sQuery(id+"F7.wireOp",EDGE,"E67")])]})]});
            fillet(context, id + "F14", {"entities" : qUnion([Q0, Q1, Q2, Q3, Q4, Q5]), "radius" : 3 * mm, "tangentPropagation" : true, "allowEdgeOverflow" : false});
        }
        {
            var Q0;
            Q0=makeQuery(id+"F1.opExtrude","CAP_EDGE",EDGE,{"disambiguationData":[OSD([sQuery(id+"F0.wireOp",EDGE,"E1.bottom")])],"isStart":false});
            fillet(context, id + "F15", {"entities" : qUnion([Q0]), "radius" : 2 * mm, "tangentPropagation" : true, "allowEdgeOverflow" : false});
        }
        {
            var Q0;
            {var subQ0=sQuery(id+"F0.wireOp",EDGE,"E21.filletArc");var subQ1=sQuery(id+"F0.wireOp",EDGE,"E7");var subQ2=sQuery(id+"F0.wireOp",EDGE,"E6");var subQ3=sQuery(id+"F0.wireOp",EDGE,"E5");var subQ4=sQuery(id+"F0.wireOp",EDGE,"E4");var subQ5=sQuery(id+"F0.wireOp",EDGE,"E22.filletArc");var subQ6=sQuery(id+"F0.wireOp",EDGE,"E1.bottom");var subQ7=sQuery(id+"F0.wireOp",EDGE,"E1.right");var subQ8=sQuery(id+"F0.wireOp",EDGE,"E1.top");var subQ9=sQuery(id+"F0.wireOp",EDGE,"E1.left");var subQ10=sQuery(id+"F0.wireOp",EDGE,"E23.filletArc");var subQ11=sQuery(id+"F0.wireOp",EDGE,"E24.filletArc");Q0=makeQuery(id+"F2.boolean.opBoolean","SPLIT",FACE,{"disambiguationData":[TD([makeQuery(id+"F1.opExtrude","SWEPT_FACE",FACE,{"disambiguationData":[OSD([subQ6])]})])],"derivedFrom":makeQuery(id+"F1.opExtrude","CAP_FACE",FACE,{"disambiguationData":[OSD([subQ6,subQ8,subQ9,subQ7,subQ4,subQ3,subQ2,subQ1,subQ0,subQ5,subQ10,subQ11])],"isStart":true})});}
            var sketch = newSketch(context, id + "F16", { "sketchPlane" : qUnion([Q0])});
            skLineSegment(sketch, "E79.0", {"start": v(-64.25, 74.25) * mm, "end": v(64.25, 74.25) * mm});
            skArc(sketch, "E80.0", {"start": v(-64.25, 74.25) * mm, "mid": v(-71.32, 71.32) * mm, "end": v(-74.25, 64.25) * mm});
            skLineSegment(sketch, "E81.0", {"start": v(-74.25, -64.25) * mm, "end": v(-74.25, 64.25) * mm});
            skArc(sketch, "E82.0", {"start": v(-74.25, -64.25) * mm, "mid": v(-71.32, -71.32) * mm, "end": v(-64.25, -74.25) * mm});
            skLineSegment(sketch, "E83.0", {"start": v(-64.25, -74.25) * mm, "end": v(64.25, -74.25) * mm});
            skArc(sketch, "E84.0", {"start": v(64.25, -74.25) * mm, "mid": v(71.32, -71.32) * mm, "end": v(74.25, -64.25) * mm});
            skLineSegment(sketch, "E85.0", {"start": v(74.25, -64.25) * mm, "end": v(74.25, 64.25) * mm});
            skArc(sketch, "E86.0", {"start": v(74.25, 64.25) * mm, "mid": v(71.32, 71.32) * mm, "end": v(64.25, 74.25) * mm});
            skArc(sketch, "E87.0", {"start": v(54.26, 47.88) * mm, "mid": v(0, 60) * mm, "end": v(-54.26, 47.88) * mm});
            skArc(sketch, "E88.0", {"start": v(60, 38.83) * mm, "mid": v(58.44, 44.2) * mm, "end": v(54.26, 47.88) * mm});
            skLineSegment(sketch, "E89.0", {"start": v(60, 38.83) * mm, "end": v(60, -38.83) * mm});
            skArc(sketch, "E90.0", {"start": v(54.26, -47.88) * mm, "mid": v(58.44, -44.2) * mm, "end": v(60, -38.83) * mm});
            skArc(sketch, "E91.0", {"start": v(-54.26, -47.88) * mm, "mid": v(0, -60) * mm, "end": v(54.26, -47.88) * mm});
            skArc(sketch, "E92.0", {"start": v(-60, -38.83) * mm, "mid": v(-58.44, -44.2) * mm, "end": v(-54.26, -47.88) * mm});
            skLineSegment(sketch, "E93.0", {"start": v(-60, 38.83) * mm, "end": v(-60, -38.83) * mm});
            skArc(sketch, "E94.0", {"start": v(-54.26, 47.88) * mm, "mid": v(-58.44, 44.2) * mm, "end": v(-60, 38.83) * mm});
            skCircle(sketch, "E95.0", {"center": v(-60, 60) * mm, "radius": 4 * mm});
            skCircle(sketch, "E96.0", {"center": v(60, 60) * mm, "radius": 4 * mm});
            skCircle(sketch, "E97.0", {"center": v(60, -60) * mm, "radius": 4 * mm});
            skCircle(sketch, "E98.0", {"center": v(-60, -60) * mm, "radius": 4 * mm});
            skLineSegment(sketch, "E99", {"start": v(0, 104.25) * mm, "end": v(0, 74.25) * mm, "construction": true});
            skPoint(sketch, "E99.startSnap0", {"position": v(0, 74.25) * mm});
            skLineSegment(sketch, "E100", {"start": v(-15, 104.25) * mm, "end": v(-15, 92.25) * mm});
            skLineSegment(sketch, "E101", {"start": v(-15, 92.25) * mm, "end": v(-33, 74.25) * mm});
            skLineSegment(sketch, "E102", {"start": v(15, 104.25) * mm, "end": v(15, 92.25) * mm});
            skLineSegment(sketch, "E103", {"start": v(15, 92.25) * mm, "end": v(33, 74.25) * mm});
            skLineSegment(sketch, "E104", {"start": v(-74.25, 0) * mm, "end": v(74.25, 0) * mm, "construction": true});
            skCircle(sketch, "E105", {"center": v(0, 104.25) * mm, "radius": 6 * mm});
            skArc(sketch, "E106", {"start": v(-15, 104.25) * mm, "mid": v(0, 119.25) * mm, "end": v(15, 104.25) * mm});
            skLineSegment(sketch, "E107.MirrorCS", {"start": v(-15, -104.25) * mm, "end": v(-15, -92.25) * mm});
            skLineSegment(sketch, "E108.MirrorCS", {"start": v(15, -104.25) * mm, "end": v(15, -92.25) * mm});
            skLineSegment(sketch, "E109.MirrorCS", {"start": v(15, -92.25) * mm, "end": v(33, -74.25) * mm});
            skLineSegment(sketch, "E110.MirrorCS", {"start": v(-15, -92.25) * mm, "end": v(-33, -74.25) * mm});
            skArc(sketch, "E111.MirrorCS", {"start": v(-15, -104.25) * mm, "mid": v(0, -119.25) * mm, "end": v(15, -104.25) * mm});
            skCircle(sketch, "E112.MirrorC", {"center": v(0, -104.25) * mm, "radius": 6 * mm});
            skLineSegment(sketch, "E113.MirrorCS", {"start": v(0, -104.25) * mm, "end": v(0, -74.25) * mm, "construction": true});
            skSolve(sketch);
        }
        {
            var Q0;
            Q0=makeQuery(id+"F16.imprint","IMPRINT",FACE,{"disambiguationData":[TD([[makeQuery(id+"F16.imprint","IMPRINT",EDGE,{"derivedFrom":sQuery(id+"F16.wireOp",EDGE,"E100")}),1.0]])]});
            var Q1;
            {var subQ1=sQuery(id+"F16.wireOp",EDGE,"E80.0");Q1=makeQuery(id+"F16.imprint","IMPRINT",FACE,{"disambiguationData":[TD([[makeQuery(id+"F16.imprint","IMPRINT",EDGE,{"derivedFrom":subQ1}),1.0]])]});}
            var Q2;
            Q2=makeQuery(id+"F16.imprint","IMPRINT",FACE,{"disambiguationData":[TD([[makeQuery(id+"F16.imprint","IMPRINT",EDGE,{"derivedFrom":sQuery(id+"F16.wireOp",EDGE,"E107.MirrorCS")}),-1.0]])]});
            var Q3;
            Q3=makeQuery(id+"F2.opExtrude","CAP_FACE",FACE,{"disambiguationData":[OSD([sQuery(id+"F0.wireOp",EDGE,"E12"),sQuery(id+"F0.wireOp",EDGE,"E13"),sQuery(id+"F0.wireOp",EDGE,"E14"),sQuery(id+"F0.wireOp",EDGE,"E15"),sQuery(id+"F0.wireOp",EDGE,"E17.filletArc"),sQuery(id+"F0.wireOp",EDGE,"E18.filletArc"),sQuery(id+"F0.wireOp",EDGE,"E19.filletArc"),sQuery(id+"F0.wireOp",EDGE,"E20.filletArc"),sQuery(id+"F0.wireOp",EDGE,"E25.0"),sQuery(id+"F0.wireOp",EDGE,"E25.1"),sQuery(id+"F0.wireOp",EDGE,"E25.2"),sQuery(id+"F0.wireOp",EDGE,"E25.3"),sQuery(id+"F0.wireOp",EDGE,"E25.4"),sQuery(id+"F0.wireOp",EDGE,"E25.5"),sQuery(id+"F0.wireOp",EDGE,"E25.6"),sQuery(id+"F0.wireOp",EDGE,"E25.7")])],"isStart":false});
            extrude(context, id + "F17", {"entities" : qUnion([Q0, Q1, Q2]), "endBound" : BoundingType.UP_TO_SURFACE, "endBoundEntityFace" : qUnion([Q3]), "depth" : 25 * mm});
        }
    });
